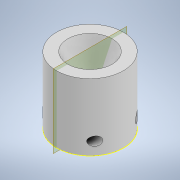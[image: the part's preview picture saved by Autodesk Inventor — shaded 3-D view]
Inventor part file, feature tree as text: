
AUTODESK INVENTOR PART (.ipt)
format: ipt  version: 2020 (Build 240168000, 168)  size: 726,528 bytes
history: native  units: in
note: dims shown in document units (in); Inventor stores cm internally (conversion verified against a paired STEP export)
features: sketch x6, revolve x2, hole x2, plane x1, thread x1, helix x1
ambient origin geometry x8: Origin, YZ Plane, XZ Plane, XY Plane, X Axis, Y Axis, Z Axis, Center Point
bodies: Solid1 (feature_tree), Solid2 (feature_tree)
feature tree (13):
  revolve  "Revolution1"  [1 undecoded]
  hole  "Hole1"  [1 undecoded]
  sketch  "Sketch3"  dims[d16=45.0deg d17=90.0deg d18=0.4in]
  plane  "Work Plane1"
  hole  "Hole2"  [1 undecoded]
  thread  "Thread1"  [1 undecoded]
  revolve  "Revolution2"  [1 undecoded]
  helix  "Coil1"  [1 undecoded]
  sketch  "Sketch1"  dims[d7=90.0deg d8=0.211in]
  sketch  "Sketch2"  dims[d10=0.375in d11=0.25in d12=0.5635in d13=0.375in d14=0.0in d15=0.325in]
  sketch  "Sketch4"  dims[d19=45.0deg d20=0.4in d21=135.0deg]
  sketch  "Sketch5"  dims[d22=0.201in d23=0.328in d24=0.332in d25=0.25in d26=0.5635in d27=0.484in d28=0.8108in]
  sketch  "Sketch6"  dims[d29=0.375in d30=0.0in d31=0.3779in d32=0.0057in d33=0.0057in d36=0.0357in d38=0.3779in d40=0.0in d41=0.0358in d42=0.4464in d43=0.3937in d44=0.0in d45=0.0in d46=0.0in d47=0.0in d48=0.0in]
note: 6 required parameter values undecoded (feature->parameter linkage not recoverable at this tier; creation-order binding heuristic only, values carry confidence <= 0.55)